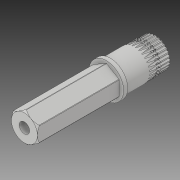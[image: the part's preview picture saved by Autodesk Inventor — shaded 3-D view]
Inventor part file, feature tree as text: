
AUTODESK INVENTOR PART (.ipt)
format: ipt  version: 2019 (Build 230136000, 136)  size: 1,382,400 bytes
history: native  units: in
note: dims shown in document units (in); Inventor stores cm internally (conversion verified against a paired STEP export)
features: fillet x1
ambient origin geometry x8: Origin, YZ Plane, XZ Plane, XY Plane, X Axis, Y Axis, Z Axis, Center Point
bodies: Solid1 (feature_tree)
feature tree (1):
  fillet  "Fillet5"  [1 undecoded]
note: 1 required parameter value undecoded (feature->parameter linkage not recoverable at this tier; creation-order binding heuristic only, values carry confidence <= 0.55)
